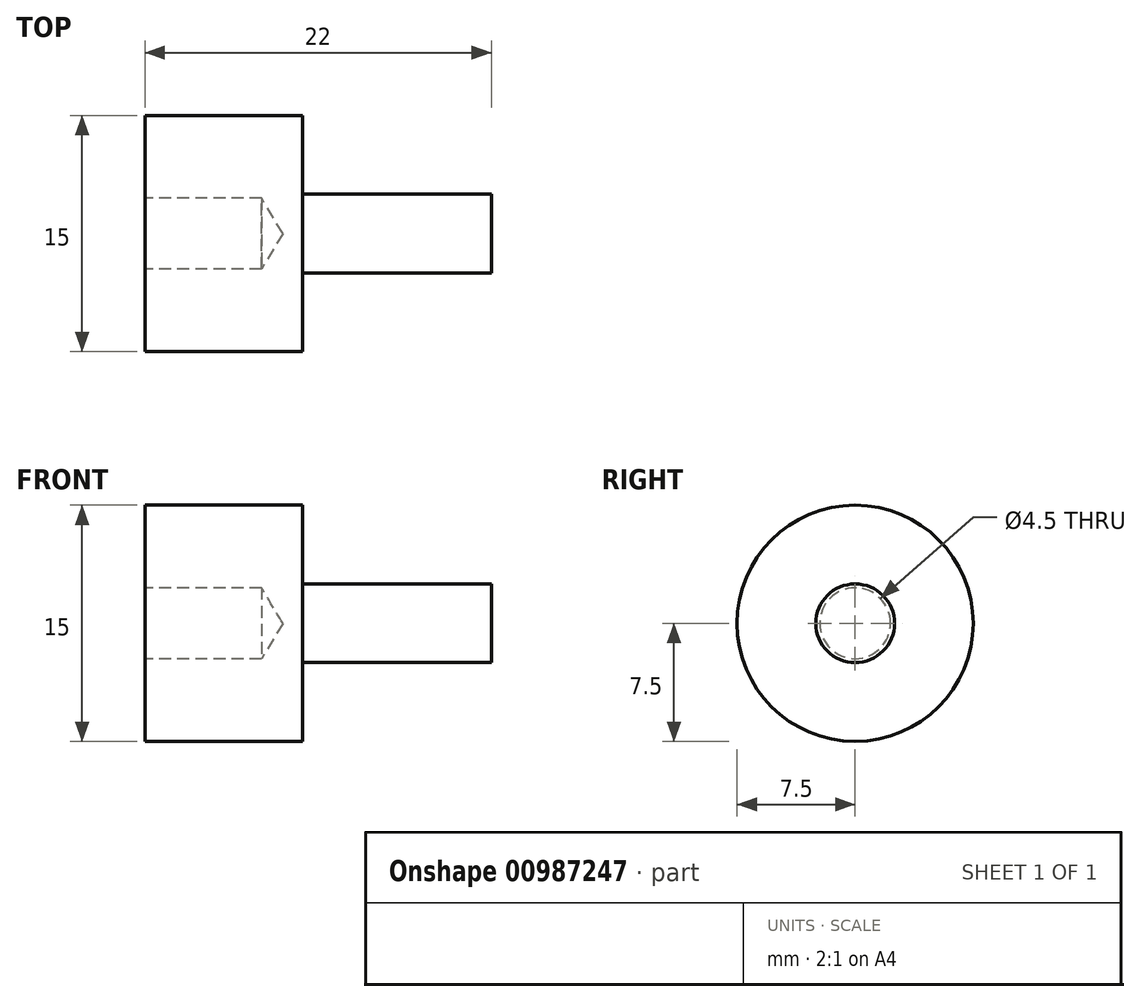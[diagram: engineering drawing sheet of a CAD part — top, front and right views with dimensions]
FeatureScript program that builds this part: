
annotation { "Feature Type Name" : "Feature", "Feature Type Description" : "" }
export const myFeature = defineFeature(function(context is Context, id is Id, definition is map)
    precondition{}
    {
        {
            var Q0;
            Q0=qCreatedBy(makeId("Front.planeOp"),FACE);
            var sketch = newSketch(context, id + "F0", { "sketchPlane" : qUnion([Q0])});
            skLineSegment(sketch, "E0", {"start": v(-10, 7.5) * mm, "end": v(0, 7.5) * mm});
            skLineSegment(sketch, "E1", {"start": v(0, 7.5) * mm, "end": v(0, 2.5) * mm});
            skLineSegment(sketch, "E2", {"start": v(0, 2.5) * mm, "end": v(12, 2.5) * mm});
            skLineSegment(sketch, "E3", {"start": v(-10, 0) * mm, "end": v(12, 0) * mm});
            skLineSegment(sketch, "E4", {"start": v(-10, 7.5) * mm, "end": v(-10, 0) * mm});
            skLineSegment(sketch, "E5", {"start": v(12, 2.5) * mm, "end": v(12, 0) * mm});
            skSolve(sketch);
        }
        {
            var Q0;
            Q0=makeQuery(id+"F0.imprint","IMPRINT",FACE,{"disambiguationData":[TD([[makeQuery(id+"F0.imprint","IMPRINT",EDGE,{"derivedFrom":sQuery(id+"F0.wireOp",EDGE,"E0")}),-1.0]])]});
            var Q1;
            Q1=sQuery(id+"F0.wireOp",EDGE,"E3");
            revolve(context, id + "F1", {"surfaceOperationType" : NewSurfaceOperationType.NEW, "entities" : qUnion([Q0]), "axis" : qUnion([Q1]), "revolveType" : RevolveType.FULL});
        }
        {
            var Q0;
            Q0=makeQuery(id+"F1.opRevolve","SWEPT_FACE",FACE,{"disambiguationData":[OSD([sQuery(id+"F0.wireOp",EDGE,"E4")])]});
            var sketch = newSketch(context, id + "F2", { "sketchPlane" : qUnion([Q0])});
            skPoint(sketch, "E6", {"position": v(0, 0) * mm});
            skSolve(sketch);
        }
        {
            var Q0;
            Q0=sQuery(id+"F2.wireOp",VERTEX,"E6");
            var Q1;
            Q1=makeQuery(id+"F1.opRevolve","SWEPT_BODY",BODY,{"disambiguationData":[OSD([sQuery(id+"F0.wireOp",EDGE,"E0"),sQuery(id+"F0.wireOp",EDGE,"E1"),sQuery(id+"F0.wireOp",EDGE,"E2"),sQuery(id+"F0.wireOp",EDGE,"E3"),sQuery(id+"F0.wireOp",EDGE,"E4"),sQuery(id+"F0.wireOp",EDGE,"E5")])]});
            hole(context, id + "F3", {"style" : HoleStyle.SIMPLE, "endStyle" : HoleEndStyle.BLIND, "standardTappedOrClearance" : lookupTablePath({ "standard" : "ISO", "engagement" : "50%", "pitch" : "0.8 mm", "size" : "M5", "type" : "Tapped" }), "standardBlindInLast" : lookupTablePath({ "standard" : "ISO", "fit" : "Normal", "engagement" : "50%", "pitch" : "0.8 mm", "size" : "M5", "type" : "Clearance & tapped" }), "holeDiameter" : 4.5 * mm, "majorDiameter" : 5 * mm, "showTappedDepth" : true, "holeDepth" : 7.4 * mm, "isTappedThrough" : true, "tappedDepth" : 5 * mm, "tapClearance" : 3, "locations" : qUnion([Q0]), "scope" : qUnion([Q1])});
        }
    });
